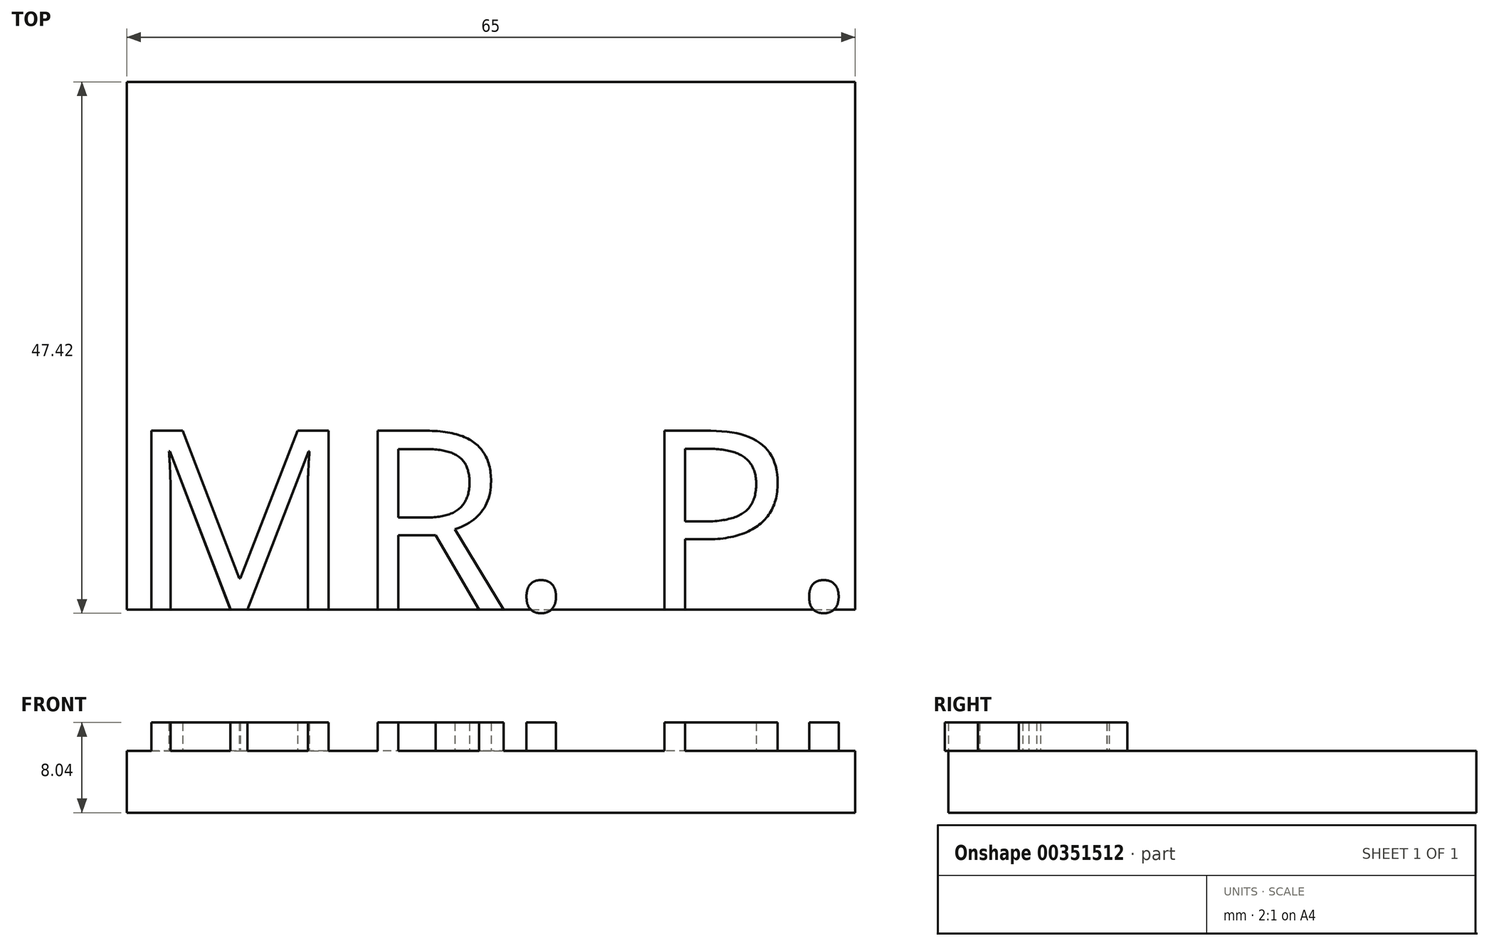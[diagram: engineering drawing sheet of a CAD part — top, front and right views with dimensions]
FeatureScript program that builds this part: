
annotation { "Feature Type Name" : "Feature", "Feature Type Description" : "" }
export const myFeature = defineFeature(function(context is Context, id is Id, definition is map)
    precondition{}
    {
        {
            var Q0;
            Q0=qCreatedBy(makeId("Top.planeOp"),FACE);
            var sketch = newSketch(context, id + "F0", { "sketchPlane" : qUnion([Q0])});
            skLineSegment(sketch, "E0.bottom", {"start": v(32.5, 23.55) * mm, "end": v(-32.5, 23.55) * mm});
            skLineSegment(sketch, "E0.top", {"start": v(32.5, -23.55) * mm, "end": v(-32.5, -23.55) * mm});
            skLineSegment(sketch, "E0.left", {"start": v(32.5, 23.55) * mm, "end": v(32.5, -23.55) * mm});
            skLineSegment(sketch, "E0.right", {"start": v(-32.5, 23.55) * mm, "end": v(-32.5, -23.55) * mm});
            skPoint(sketch, "E0.middle", {"position": v(0, 0) * mm});
            skSolve(sketch);
        }
        {
            var Q0;
            Q0 = qSketchRegion(id + "F0", true);
            extrude(context, id + "F1", {"entities" : qUnion([Q0]), "depth" : 5.5 * mm});
        }
        {
            var Q0;
            Q0=makeQuery(id+"F1.opExtrude","CAP_FACE",FACE,{"disambiguationData":[OSD([sQuery(id+"F0.wireOp",EDGE,"E0.bottom"),sQuery(id+"F0.wireOp",EDGE,"E0.top"),sQuery(id+"F0.wireOp",EDGE,"E0.left"),sQuery(id+"F0.wireOp",EDGE,"E0.right")])],"isStart":false});
            var sketch = newSketch(context, id + "F2", { "sketchPlane" : qUnion([Q0])});
            skText(sketch, "E1", { "text": "MR. P.", "fontName": "OpenSans-Regular.ttf"});
            const initialGuessF2  = {"E1": [-0.0325, -0.02355, 1, 0, 0.0161]};
            skSetInitialGuess(sketch, initialGuessF2);
            skSolve(sketch);
        }
        {
            var Q0;
            Q0 = qSketchRegion(id + "F2", true);
            extrude(context, id + "F3", {"entities" : qUnion([Q0]), "operationType" : NewBodyOperationType.ADD, "depth" : 2.54 * mm});
        }
    });
